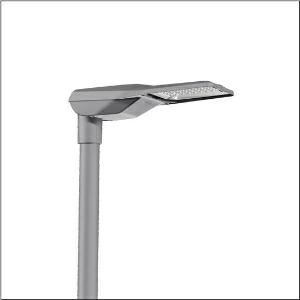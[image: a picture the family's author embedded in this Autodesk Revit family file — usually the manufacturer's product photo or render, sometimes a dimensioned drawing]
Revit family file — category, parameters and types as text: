
# Revit family: streetlight_sl_21_iq_mini___st0_8a_5xe2c41g08hb_fab9
name_source: partatom
category: Lighting Fixtures
units: mm (PartAtom-declared; Revit-internal decimal feet)

## family parameters
Cut with Voids When Loaded = No
Host = Face
Light Source = No
Part Type = Normal
Room Calculation Point = No
Round Connector Dimension = Use Diameter
Shared = No

## types (1)
- --- (1 x LED, 9860 lm, 70.9 W, 4000K)
    Apparent Load = 71 VA
    CIE Flux Codes = 38 75 97 100 100
    Color Rendering = 70
    Color Temperature = 4000K
    Default Elevation = 1800 mm
    Description = Streetlight SL 21 iQ mini, mast luminaire, primary light control with lens, of PMMA, primary optical cover: cover, of toughened safety glass, transparent, light distribution: ST0.8a, light emission: direct distribution, primary light characteristic: asymmetric, installation type: post-top, side-entry, LED, High Power LED, rated luminous flux: 9.860lm, luminous efficacy: 139lm/W, light colour: 740, colour temperature: 4000K, control: Street-Remote, Auto-Match, Temp-Guard, Lumen-Switch, Night-Set, Smart-Wire, Light-Fading, Desk-Remote (wireless, voltage-free reading and setting of iQ features in the workshop via application-optimized NFC function/RFID function), optimised constant luminous flux control (CLO 2.0), presetting dimming linear, mains connection: 220..240V, AC, 50/60Hz, start of lifetime: 71W, end of service life: 75W, reduction: 31W, luminaire housing, of diecast aluminium, powder-coated, Siteco® metallic grey (DB 702S), corrosivity category C5 mid according to DIN EN ISO 12944, please order mast flange separately, inclination adjustable: 0°, 5°, 10°, 15°, sealing non-destructively replaceable, multi-level sealing system, length: 628mm, width: 235mm, height: 110mm, mast flange for spigot size: 42mm (side-entry): 5XC10008XM4, 60/48mm (side-entry/post-top): 5XC10108XM2, 76/60mm (side-entry/post-top): 5XC10108XM1, protection rating (complete): IP66, insulation class (complete): insulation class II (safety insulation), certification: CE, ENEC, ENEC+, VDE, impact resistance: IK09, permissible operating ambient temperature for outdoor applications: -40..+50°C, standard-compliant lighting for roads and squares, packaging unit: 1 piece

Light Distribution: ST0.8a
    Height = 110 mm
    Lamp = 1 x LED
    Lamp Light Flux = 9860 lm
    Lamp Power = 70.9 W
    Lamp count = 1
    Length = 625 mm
    Luminous efficacy = 139 lm/W
    Manufacturer = Siteco
    ModVariant = No
    Model = 5XE2C41G08HB
    Number of Poles = 1
    OnlyDefault = Yes
    Power Factor = 1
    Product Name = Streetlight SL 21 iQ mini | ST0.8a
    Product group = mast luminaire | pylon top
    ProductGroupID = 6100
    Protection Class = Protection class II
    Protection Degree = IP 66
    RLX_Detail_Level = 1
    RLX_Emergency_Light_Flux = 0 lm
    RLX_Emergency_Type = 0
    RLX_Emergency_Type_DB = No
    RlxData = <blob elided: 93437 chars, md5=fdc76322>
    Socket = socket
    Standby Power = 0 W
    System Light Flux = 9860 lm
    System Power = 71 W
    Type Comments = factory setting: luminous flux: 100 % | dim-lin: 254 | 711 mA
    Type Image = l_1003519.jpg
    URL = http://relux.com
    VarID = @adj_089659
    Voltage = 0 V
    Weight = 0.00 kg
    Width = 234 mm

## geometry (parser evidence)
native form markers: Blend x4, Sweep x10
no freeform markers — native parametric forms only
